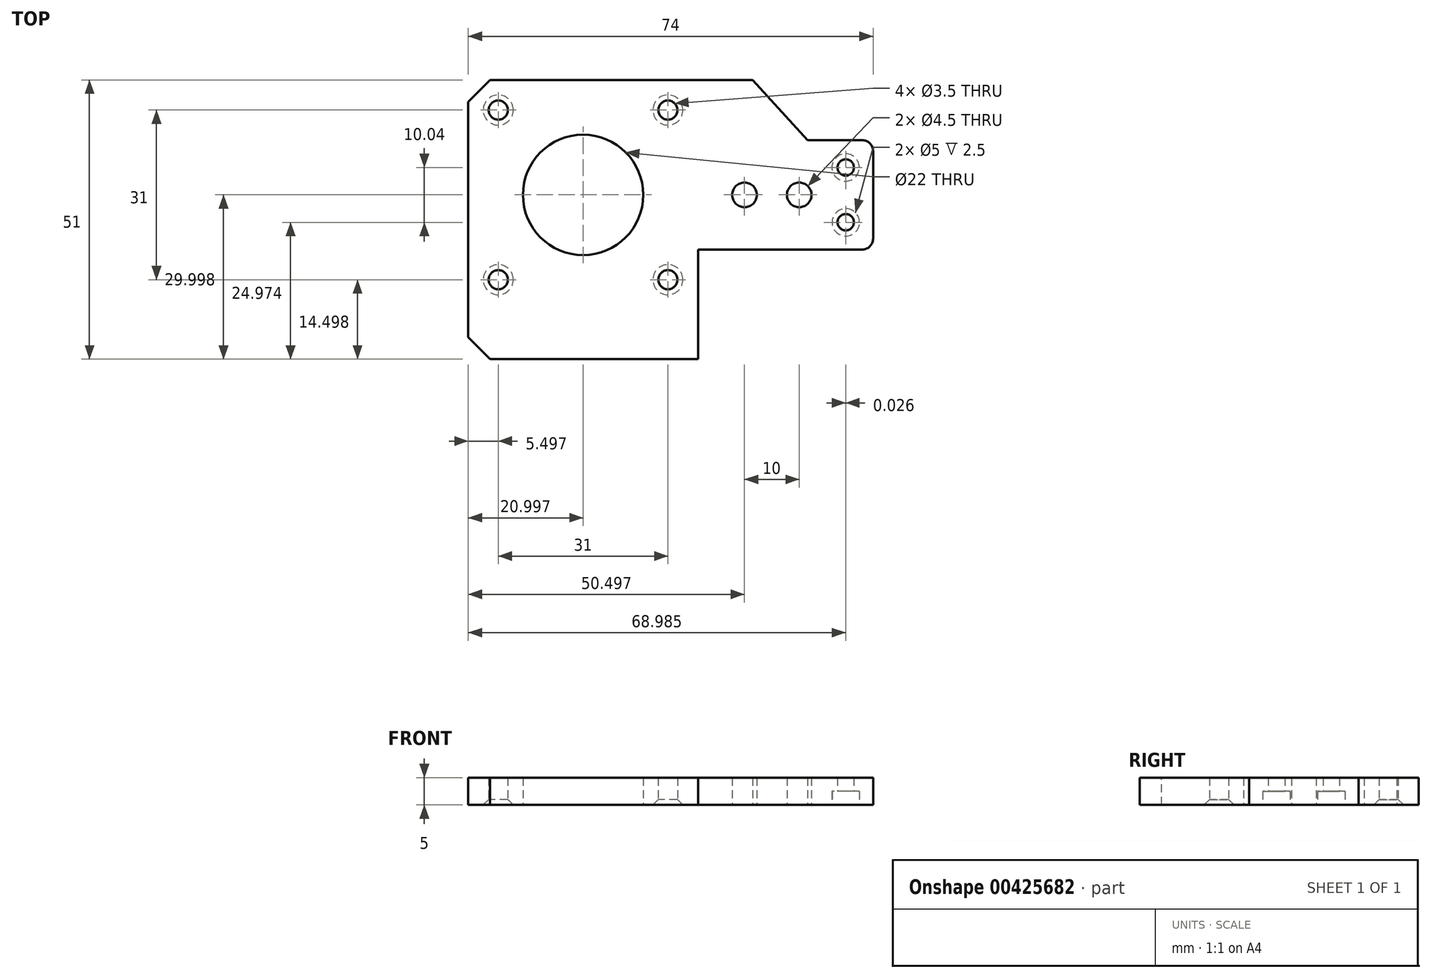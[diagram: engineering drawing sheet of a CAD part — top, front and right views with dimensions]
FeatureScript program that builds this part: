
annotation { "Feature Type Name" : "Feature", "Feature Type Description" : "" }
export const myFeature = defineFeature(function(context is Context, id is Id, definition is map)
    precondition{}
    {
        {
            var Q0;
            Q0=qCreatedBy(makeId("Top.planeOp"),FACE);
            var sketch = newSketch(context, id + "F0", { "sketchPlane" : qUnion([Q0])});
            skLineSegment(sketch, "E0.bottom", {"start": v(-29.12, 25.58) * mm, "end": v(12.88, 25.58) * mm});
            skLineSegment(sketch, "E0.top", {"start": v(-29.12, -25.42) * mm, "end": v(12.88, -25.42) * mm});
            skLineSegment(sketch, "E0.left", {"start": v(-29.12, 25.58) * mm, "end": v(-29.12, -25.42) * mm});
            skLineSegment(sketch, "E0.right", {"start": v(12.88, 25.58) * mm, "end": v(12.88, -25.42) * mm});
            skLineSegment(sketch, "E1", {"start": v(-51.12, -5.42) * mm, "end": v(63.52, -5.42) * mm, "construction": true});
            skLineSegment(sketch, "E2", {"start": v(-50.26, 14.58) * mm, "end": v(65.58, 14.58) * mm, "construction": true});
            skLineSegment(sketch, "E3", {"start": v(32.88, 48.45) * mm, "end": v(32.88, -32.1) * mm, "construction": true});
            skLineSegment(sketch, "E4", {"start": v(22.88, 49.32) * mm, "end": v(22.88, -46.56) * mm, "construction": true});
            skLineSegment(sketch, "E5", {"start": v(12.88, 25.58) * mm, "end": v(22.88, 25.58) * mm});
            skLineSegment(sketch, "E6", {"start": v(22.88, 25.58) * mm, "end": v(32.88, 14.58) * mm});
            skLineSegment(sketch, "E7", {"start": v(32.88, 14.58) * mm, "end": v(44.88, 14.58) * mm});
            skLineSegment(sketch, "E8", {"start": v(44.88, 14.58) * mm, "end": v(44.88, -5.42) * mm});
            skLineSegment(sketch, "E9", {"start": v(44.88, -5.42) * mm, "end": v(12.88, -5.42) * mm});
            skCircle(sketch, "E10", {"center": v(-8.12, 4.58) * mm, "radius": 11 * mm});
            skCircle(sketch, "E11", {"center": v(-23.62, 20.08) * mm, "radius": 1.75 * mm});
            skLineSegment(sketch, "E12", {"start": v(-23.62, 20.08) * mm, "end": v(7.38, 20.08) * mm, "construction": true});
            skLineSegment(sketch, "E13", {"start": v(7.38, 20.08) * mm, "end": v(7.38, -10.92) * mm, "construction": true});
            skLineSegment(sketch, "E14", {"start": v(7.38, -10.92) * mm, "end": v(-23.62, -10.92) * mm, "construction": true});
            skLineSegment(sketch, "E15", {"start": v(-23.62, -10.92) * mm, "end": v(-23.62, 20.08) * mm, "construction": true});
            skCircle(sketch, "E16", {"center": v(7.38, 20.08) * mm, "radius": 1.75 * mm});
            skCircle(sketch, "E17", {"center": v(7.38, -10.92) * mm, "radius": 1.75 * mm});
            skCircle(sketch, "E18", {"center": v(-23.62, -10.92) * mm, "radius": 1.75 * mm});
            skCircle(sketch, "E19", {"center": v(21.38, 4.58) * mm, "radius": 2.25 * mm});
            skCircle(sketch, "E20", {"center": v(31.38, 4.58) * mm, "radius": 2.25 * mm});
            skCircle(sketch, "E21", {"center": v(39.88, -0.42) * mm, "radius": 1.5 * mm});
            skCircle(sketch, "E22", {"center": v(39.88, 9.58) * mm, "radius": 1.5 * mm});
            skSolve(sketch);
        }
        {
            var Q0;
            {var subQ1=sQuery(id+"F0.wireOp",EDGE,"E0.bottom");Q0=makeQuery(id+"F0.imprint","IMPRINT",FACE,{"disambiguationData":[TD([[makeQuery(id+"F0.imprint","IMPRINT",EDGE,{"derivedFrom":subQ1}),-1.0]])]});}
            var Q1;
            {var subQ0=sQuery(id+"F0.wireOp",EDGE,"E5");Q1=makeQuery(id+"F0.imprint","IMPRINT",FACE,{"disambiguationData":[TD([[makeQuery(id+"F0.imprint","IMPRINT",EDGE,{"derivedFrom":subQ0}),-1.0]])]});}
            extrude(context, id + "F1", {"entities" : qUnion([Q0, Q1]), "depth" : 5 * mm});
        }
        {
            var Q0;
            Q0=makeQuery(id+"F0.imprint","IMPRINT",FACE,{"disambiguationData":[TD([[makeQuery(id+"F0.imprint","IMPRINT",EDGE,{"derivedFrom":sQuery(id+"F0.wireOp",EDGE,"E21")}),1.0]])]});
            var sketch = newSketch(context, id + "F2", { "sketchPlane" : qUnion([Q0])});
            skCircle(sketch, "E23", {"center": v(39.86, 9.6) * mm, "radius": 2.5 * mm});
            skCircle(sketch, "E24", {"center": v(39.9, -0.45) * mm, "radius": 2.5 * mm});
            skSolve(sketch);
        }
        {
            var Q0;
            Q0=makeQuery(id+"F2.imprint","IMPRINT",FACE,{"disambiguationData":[TD([[makeQuery(id+"F2.imprint","IMPRINT",EDGE,{"derivedFrom":sQuery(id+"F2.wireOp",EDGE,"E24")}),1.0]])]});
            var Q1;
            Q1=makeQuery(id+"F2.imprint","IMPRINT",FACE,{"disambiguationData":[TD([[makeQuery(id+"F2.imprint","IMPRINT",EDGE,{"derivedFrom":sQuery(id+"F2.wireOp",EDGE,"E23")}),1.0]])]});
            extrude(context, id + "F3", {"entities" : qUnion([Q0, Q1]), "operationType" : NewBodyOperationType.REMOVE, "oppositeDirection" : true, "depth" : -2.5 * mm});
        }
        {
            var Q0;
            Q0=makeQuery(id+"F1.opExtrude","CAP_EDGE",EDGE,{"disambiguationData":[OSD([sQuery(id+"F0.wireOp",EDGE,"E11")])],"isStart":true});
            var Q1;
            Q1=makeQuery(id+"F1.opExtrude","CAP_EDGE",EDGE,{"disambiguationData":[OSD([sQuery(id+"F0.wireOp",EDGE,"E16")])],"isStart":true});
            var Q2;
            Q2=makeQuery(id+"F1.opExtrude","CAP_EDGE",EDGE,{"disambiguationData":[OSD([sQuery(id+"F0.wireOp",EDGE,"E17")])],"isStart":true});
            var Q3;
            Q3=makeQuery(id+"F1.opExtrude","CAP_EDGE",EDGE,{"disambiguationData":[OSD([sQuery(id+"F0.wireOp",EDGE,"E18")])],"isStart":true});
            chamfer(context, id + "F4", {"entities" : qUnion([Q0, Q1, Q2, Q3]), "width" : 1 * mm, "tangentPropagation" : true});
        }
        {
            var Q0;
            Q0=makeQuery(id+"F1.opExtrude","SWEPT_EDGE",EDGE,{"disambiguationData":[OSD([sQuery(id+"F0.wireOp",EDGE,"E0.bottom"),sQuery(id+"F0.wireOp",EDGE,"E0.left")])]});
            var Q1;
            Q1=makeQuery(id+"F1.opExtrude","SWEPT_EDGE",EDGE,{"disambiguationData":[OSD([sQuery(id+"F0.wireOp",EDGE,"E0.top"),sQuery(id+"F0.wireOp",EDGE,"E0.left")])]});
            chamfer(context, id + "F5", {"entities" : qUnion([Q0, Q1]), "width" : 4 * mm, "tangentPropagation" : true});
        }
        {
            var Q0;
            Q0=makeQuery(id+"F1.opExtrude","SWEPT_EDGE",EDGE,{"disambiguationData":[OSD([sQuery(id+"F0.wireOp",EDGE,"E7"),sQuery(id+"F0.wireOp",EDGE,"E8")])]});
            var Q1;
            Q1=makeQuery(id+"F1.opExtrude","SWEPT_EDGE",EDGE,{"disambiguationData":[OSD([sQuery(id+"F0.wireOp",EDGE,"E8"),sQuery(id+"F0.wireOp",EDGE,"E9")])]});
            fillet(context, id + "F6", {"entities" : qUnion([Q0, Q1]), "radius" : 2 * mm, "tangentPropagation" : true, "allowEdgeOverflow" : false});
        }
    });
